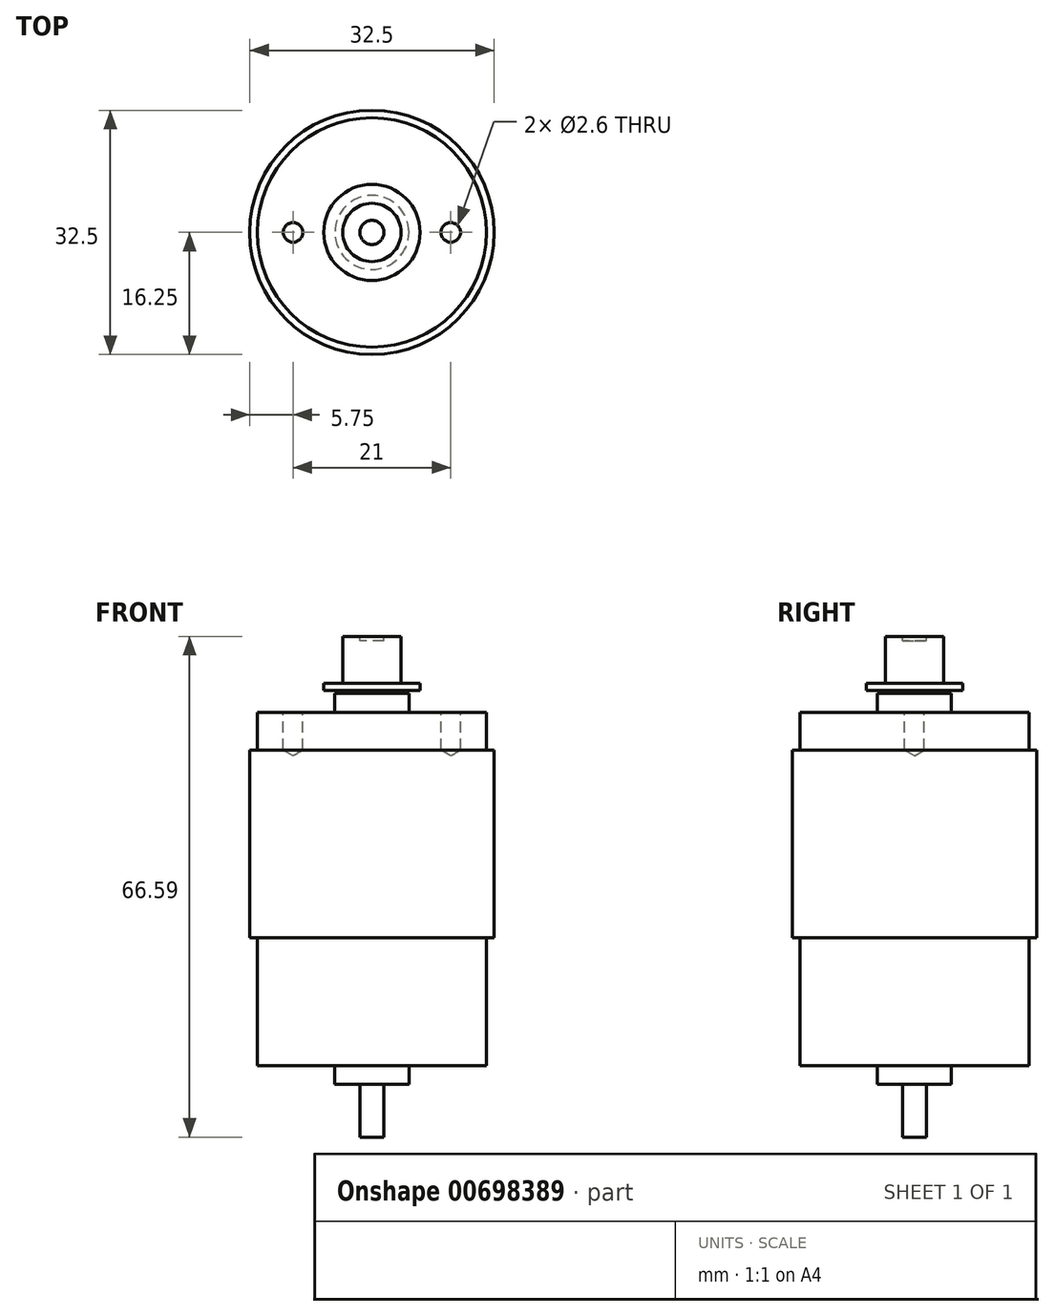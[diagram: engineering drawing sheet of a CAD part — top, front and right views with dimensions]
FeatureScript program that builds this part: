
annotation { "Feature Type Name" : "Feature", "Feature Type Description" : "" }
export const myFeature = defineFeature(function(context is Context, id is Id, definition is map)
    precondition{}
    {
        {
            var Q0;
            Q0=qCreatedBy(makeId("Front.planeOp"),FACE);
            var sketch = newSketch(context, id + "F0", { "sketchPlane" : qUnion([Q0])});
            skLineSegment(sketch, "E0", {"start": v(0, 33) * mm, "end": v(0, -33) * mm});
            skLineSegment(sketch, "E1", {"start": v(0, 33) * mm, "end": v(1.6, 33) * mm});
            skLineSegment(sketch, "E2", {"start": v(1.6, 33) * mm, "end": v(1.6, 26) * mm});
            skLineSegment(sketch, "E3", {"start": v(1.6, 26) * mm, "end": v(4.93, 26) * mm});
            skLineSegment(sketch, "E4", {"start": v(4.93, 26) * mm, "end": v(4.93, 23.5) * mm});
            skLineSegment(sketch, "E5", {"start": v(4.93, 23.5) * mm, "end": v(15.25, 23.5) * mm});
            skLineSegment(sketch, "E6", {"start": v(15.25, 23.5) * mm, "end": v(15.25, 18.5) * mm});
            skLineSegment(sketch, "E7", {"start": v(15.25, -23.5) * mm, "end": v(4.92, -23.5) * mm});
            skLineSegment(sketch, "E8", {"start": v(4.92, -23.5) * mm, "end": v(4.92, -26) * mm});
            skLineSegment(sketch, "E9", {"start": v(4.92, -26) * mm, "end": v(1.6, -26) * mm});
            skLineSegment(sketch, "E10", {"start": v(1.6, -26) * mm, "end": v(1.6, -33) * mm});
            skLineSegment(sketch, "E11", {"start": v(1.6, -33) * mm, "end": v(0, -33) * mm});
            skLineSegment(sketch, "E12", {"start": v(15.25, -6.5) * mm, "end": v(15.25, -23.5) * mm});
            skLineSegment(sketch, "E13", {"start": v(15.25, 18.5) * mm, "end": v(16.25, 18.5) * mm});
            skLineSegment(sketch, "E14", {"start": v(16.25, 18.5) * mm, "end": v(16.25, -6.5) * mm});
            skLineSegment(sketch, "E15", {"start": v(16.25, -6.5) * mm, "end": v(15.25, -6.5) * mm});
            skSolve(sketch);
        }
        {
            var Q0;
            Q0 = qSketchRegion(id + "F0", true);
            var Q1;
            Q1=sQuery(id+"F0.wireOp",EDGE,"E0");
            revolve(context, id + "F1", {"entities" : qUnion([Q0]), "axis" : qUnion([Q1]), "revolveType" : RevolveType.FULL});
        }
        {
            var Q0;
            Q0=makeQuery(id+"F1.opRevolve","SWEPT_FACE",FACE,{"disambiguationData":[OSD([sQuery(id+"F0.wireOp",EDGE,"E5")])]});
            var sketch = newSketch(context, id + "F2", { "sketchPlane" : qUnion([Q0])});
            skPoint(sketch, "E16", {"position": v(10.5, 0) * mm});
            skPoint(sketch, "E17.1.0", {"position": v(-10.5, 0) * mm});
            skPoint(sketch, "E17.center", {"position": v(0, 0) * mm});
            skSolve(sketch);
        }
        {
            var Q0;
            Q0=sQuery(id+"F2.wireOp",VERTEX,"E17.1.0");
            var Q1;
            Q1=sQuery(id+"F2.wireOp",VERTEX,"E16");
            var Q2;
            Q2=makeQuery(id+"F1.opRevolve","SWEPT_BODY",BODY,{"disambiguationData":[OSD([sQuery(id+"F0.wireOp",EDGE,"E0"),sQuery(id+"F0.wireOp",EDGE,"E1"),sQuery(id+"F0.wireOp",EDGE,"E2"),sQuery(id+"F0.wireOp",EDGE,"E3"),sQuery(id+"F0.wireOp",EDGE,"E4"),sQuery(id+"F0.wireOp",EDGE,"E5"),sQuery(id+"F0.wireOp",EDGE,"E6"),sQuery(id+"F0.wireOp",EDGE,"E7"),sQuery(id+"F0.wireOp",EDGE,"E8"),sQuery(id+"F0.wireOp",EDGE,"E9"),sQuery(id+"F0.wireOp",EDGE,"E10"),sQuery(id+"F0.wireOp",EDGE,"E11"),sQuery(id+"F0.wireOp",EDGE,"E12"),sQuery(id+"F0.wireOp",EDGE,"E13"),sQuery(id+"F0.wireOp",EDGE,"E14"),sQuery(id+"F0.wireOp",EDGE,"E15")])]});
            hole(context, id + "F3", {"style" : HoleStyle.SIMPLE, "endStyle" : HoleEndStyle.BLIND, "holeDiameter" : 2.6 * mm, "majorDiameter" : 5 * mm, "holeDepth" : 5 * mm, "isTappedThrough" : true, "tappedDepth" : 12 * mm, "tapClearance" : 3, "locations" : qUnion([Q0, Q1]), "scope" : qUnion([Q2])});
        }
        {
            var Q0;
            Q0=qCreatedBy(makeId("Front.planeOp"),FACE);
            var sketch = newSketch(context, id + "F4", { "sketchPlane" : qUnion([Q0])});
            skLineSegment(sketch, "E18", {"start": v(3.87, 33.59) * mm, "end": v(3.87, 27.39) * mm});
            skLineSegment(sketch, "E19", {"start": v(3.87, 27.39) * mm, "end": v(6.4, 27.39) * mm});
            skLineSegment(sketch, "E20", {"start": v(6.4, 27.39) * mm, "end": v(6.4, 26.39) * mm});
            skLineSegment(sketch, "E21", {"start": v(6.4, 26.39) * mm, "end": v(1.6, 26.39) * mm});
            skLineSegment(sketch, "E22", {"start": v(1.6, 26.39) * mm, "end": v(1.6, 33.59) * mm});
            skLineSegment(sketch, "E23", {"start": v(1.6, 33.59) * mm, "end": v(3.87, 33.59) * mm});
            skSolve(sketch);
        }
        {
            var Q0;
            Q0 = qSketchRegion(id + "F4", true);
            var Q1;
            Q1=sQuery(id+"F0.wireOp",EDGE,"E0");
            revolve(context, id + "F5", {"operationType" : NewBodyOperationType.ADD, "surfaceOperationType" : NewSurfaceOperationType.NEW, "entities" : qUnion([Q0]), "axis" : qUnion([Q1]), "revolveType" : RevolveType.FULL});
        }
    });
